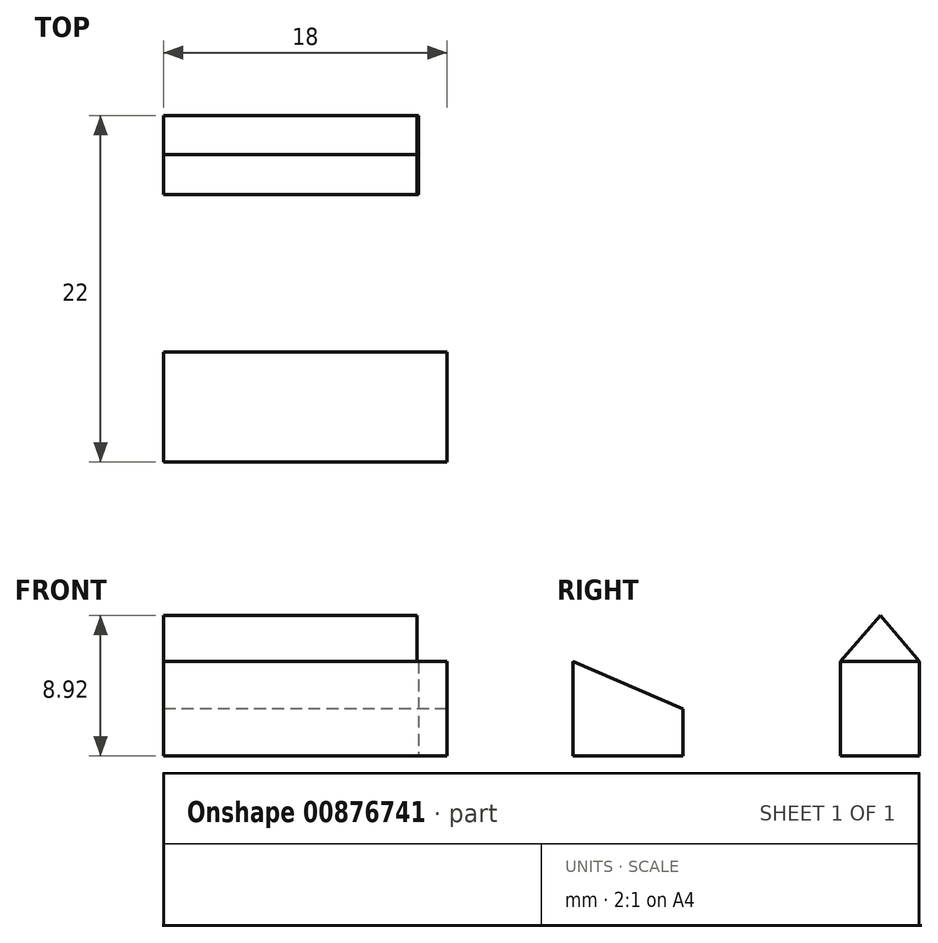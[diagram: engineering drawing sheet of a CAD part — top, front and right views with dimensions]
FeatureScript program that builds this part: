
annotation { "Feature Type Name" : "Feature", "Feature Type Description" : "" }
export const myFeature = defineFeature(function(context is Context, id is Id, definition is map)
    precondition{}
    {
        {
            var Q0;
            Q0=qCreatedBy(makeId("Top.planeOp"),FACE);
            var sketch = newSketch(context, id + "F0", { "sketchPlane" : qUnion([Q0])});
            skLineSegment(sketch, "E0.bottom", {"start": v(9, -12.5) * mm, "end": v(-9, -12.5) * mm});
            skLineSegment(sketch, "E0.top", {"start": v(9, 12.5) * mm, "end": v(-9, 12.5) * mm});
            skLineSegment(sketch, "E0.left", {"start": v(9, -12.5) * mm, "end": v(9, 12.5) * mm});
            skLineSegment(sketch, "E0.right", {"start": v(-9, -12.5) * mm, "end": v(-9, 12.5) * mm});
            skPoint(sketch, "E0.middle", {"position": v(0, 0) * mm});
            skLineSegment(sketch, "E1", {"start": v(0, -12.5) * mm, "end": v(0, -9.5) * mm, "construction": true});
            skLineSegment(sketch, "E2", {"start": v(9, -9.5) * mm, "end": v(-9, -9.5) * mm});
            skLineSegment(sketch, "E3", {"start": v(0, -9.5) * mm, "end": v(0, -2.5) * mm, "construction": true});
            skLineSegment(sketch, "E4", {"start": v(9, -2.5) * mm, "end": v(-9, -2.5) * mm});
            skLineSegment(sketch, "E5", {"start": v(-9, -9.5) * mm, "end": v(-5.4, -9.5) * mm, "construction": true});
            skLineSegment(sketch, "E6", {"start": v(-5.4, -9.5) * mm, "end": v(-1.8, -9.5) * mm, "construction": true});
            skLineSegment(sketch, "E7", {"start": v(-1.8, -9.5) * mm, "end": v(1.8, -9.5) * mm, "construction": true});
            skLineSegment(sketch, "E8", {"start": v(-5.4, -9.5) * mm, "end": v(-5.4, -2.5) * mm});
            skLineSegment(sketch, "E9", {"start": v(-1.8, -9.5) * mm, "end": v(-1.8, -2.5) * mm});
            skLineSegment(sketch, "E10.MirrorCS", {"start": v(1.8, -9.5) * mm, "end": v(1.8, -2.5) * mm});
            skLineSegment(sketch, "E11.MirrorCS", {"start": v(5.4, -9.5) * mm, "end": v(5.4, -2.5) * mm});
            skLineSegment(sketch, "E12", {"start": v(-9, 12.5) * mm, "end": v(-9, 7.5) * mm, "construction": true});
            skLineSegment(sketch, "E13", {"start": v(-9, 7.5) * mm, "end": v(9, 7.5) * mm});
            skLineSegment(sketch, "E14", {"start": v(9, 7.5) * mm, "end": v(7.2, 7.5) * mm, "construction": true});
            skLineSegment(sketch, "E15", {"start": v(7.2, 7.5) * mm, "end": v(7.2, 12.5) * mm});
            skSolve(sketch);
        }
        {
            var Q0;
            {var subQ3=sQuery(id+"F0.wireOp",EDGE,"E15");Q0=makeQuery(id+"F0.imprint","IMPRINT",FACE,{"disambiguationData":[TD([[makeQuery(id+"F0.imprint","IMPRINT",EDGE,{"derivedFrom":subQ3}),1.0]])]});}
            var Q1;
            {var subQ5=sQuery(id+"F0.wireOp",EDGE,"E8");Q1=makeQuery(id+"F0.imprint","IMPRINT",FACE,{"disambiguationData":[TD([[makeQuery(id+"F0.imprint","IMPRINT",EDGE,{"derivedFrom":subQ5}),1.0]])]});}
            var Q2;
            {var subQ0=sQuery(id+"F0.wireOp",EDGE,"E8");Q2=makeQuery(id+"F0.imprint","IMPRINT",FACE,{"disambiguationData":[TD([[makeQuery(id+"F0.imprint","IMPRINT",EDGE,{"derivedFrom":subQ0}),-1.0]])]});}
            var Q3;
            {var subQ0=sQuery(id+"F0.wireOp",EDGE,"E9");Q3=makeQuery(id+"F0.imprint","IMPRINT",FACE,{"disambiguationData":[TD([[makeQuery(id+"F0.imprint","IMPRINT",EDGE,{"derivedFrom":subQ0}),-1.0]])]});}
            var Q4;
            {var subQ0=sQuery(id+"F0.wireOp",EDGE,"E10.MirrorCS");Q4=makeQuery(id+"F0.imprint","IMPRINT",FACE,{"disambiguationData":[TD([[makeQuery(id+"F0.imprint","IMPRINT",EDGE,{"derivedFrom":subQ0}),-1.0]])]});}
            var Q5;
            {var subQ5=sQuery(id+"F0.wireOp",EDGE,"E11.MirrorCS");Q5=makeQuery(id+"F0.imprint","IMPRINT",FACE,{"disambiguationData":[TD([[makeQuery(id+"F0.imprint","IMPRINT",EDGE,{"derivedFrom":subQ5}),-1.0]])]});}
            extrude(context, id + "F1", {"entities" : qUnion([Q0, Q1, Q2, Q3, Q4, Q5]), "depth" : 6 * mm, "offsetDistance" : 25 * mm});
        }
        {
            var Q0;
            {var subQ0=sQuery(id+"F0.wireOp",EDGE,"E0.right");Q0=makeQuery(id+"F1.opExtrude","SWEPT_FACE",FACE,{"disambiguationData":[OSD([subQ0]),TDD([makeQuery(id+"F0.imprint","IMPRINT",EDGE,{"disambiguationData":[TD([[makeQuery(id+"F0.imprint","INTERSECT",VERTEX,{"derivedFrom":[subQ0,sQuery(id+"F0.wireOp",EDGE,"E2")]}),-1.0]])],"derivedFrom":subQ0})])]});}
            var sketch = newSketch(context, id + "F2", { "sketchPlane" : qUnion([Q0])});
            skLineSegment(sketch, "E16", {"start": v(9.5, 6) * mm, "end": v(2.5, 3) * mm});
            skSolve(sketch);
        }
        {
            var Q0;
            Q0 = qSketchRegion(id + "F2", true);
            var Q1;
            {var subQ0=sQuery(id+"F2.wireOp",EDGE,"E16");Q1=makeQuery(id+"F2.imprint","IMPRINT",FACE,{"disambiguationData":[TD([[makeQuery(id+"F2.imprint","IMPRINT",EDGE,{"derivedFrom":subQ0}),-1.0]])]});}
            extrude(context, id + "F3", {"entities" : qUnion([Q0, Q1]), "operationType" : NewBodyOperationType.REMOVE, "oppositeDirection" : true, "depth" : 25 * mm, "offsetDistance" : 25 * mm});
        }
        {
            var Q0;
            {var subQ0=sQuery(id+"F0.wireOp",EDGE,"E0.right");Q0=makeQuery(id+"F1.opExtrude","SWEPT_FACE",FACE,{"disambiguationData":[OSD([subQ0]),TDD([makeQuery(id+"F0.imprint","IMPRINT",EDGE,{"disambiguationData":[TD([[makeQuery(id+"F0.imprint","INTERSECT",VERTEX,{"derivedFrom":[sQuery(id+"F0.wireOp",EDGE,"E0.top"),subQ0]}),1.0]])],"derivedFrom":subQ0})])]});}
            var sketch = newSketch(context, id + "F4", { "sketchPlane" : qUnion([Q0])});
            skLineSegment(sketch, "E17", {"start": v(-12.5, 6) * mm, "end": v(-10.04, 8.92) * mm});
            skLineSegment(sketch, "E18", {"start": v(-10.04, 8.92) * mm, "end": v(-7.5, 6) * mm});
            skSolve(sketch);
        }
        {
            var Q0;
            Q0=makeQuery(id+"F4.imprint","IMPRINT",FACE,{"disambiguationData":[TD([[makeQuery(id+"F4.imprint","IMPRINT",EDGE,{"derivedFrom":sQuery(id+"F4.wireOp",EDGE,"E17")}),-1.0]])]});
            extrude(context, id + "F5", {"entities" : qUnion([Q0]), "operationType" : NewBodyOperationType.ADD, "oppositeDirection" : true, "depth" : 16.1 * mm, "offsetDistance" : 25 * mm});
        }
    });
